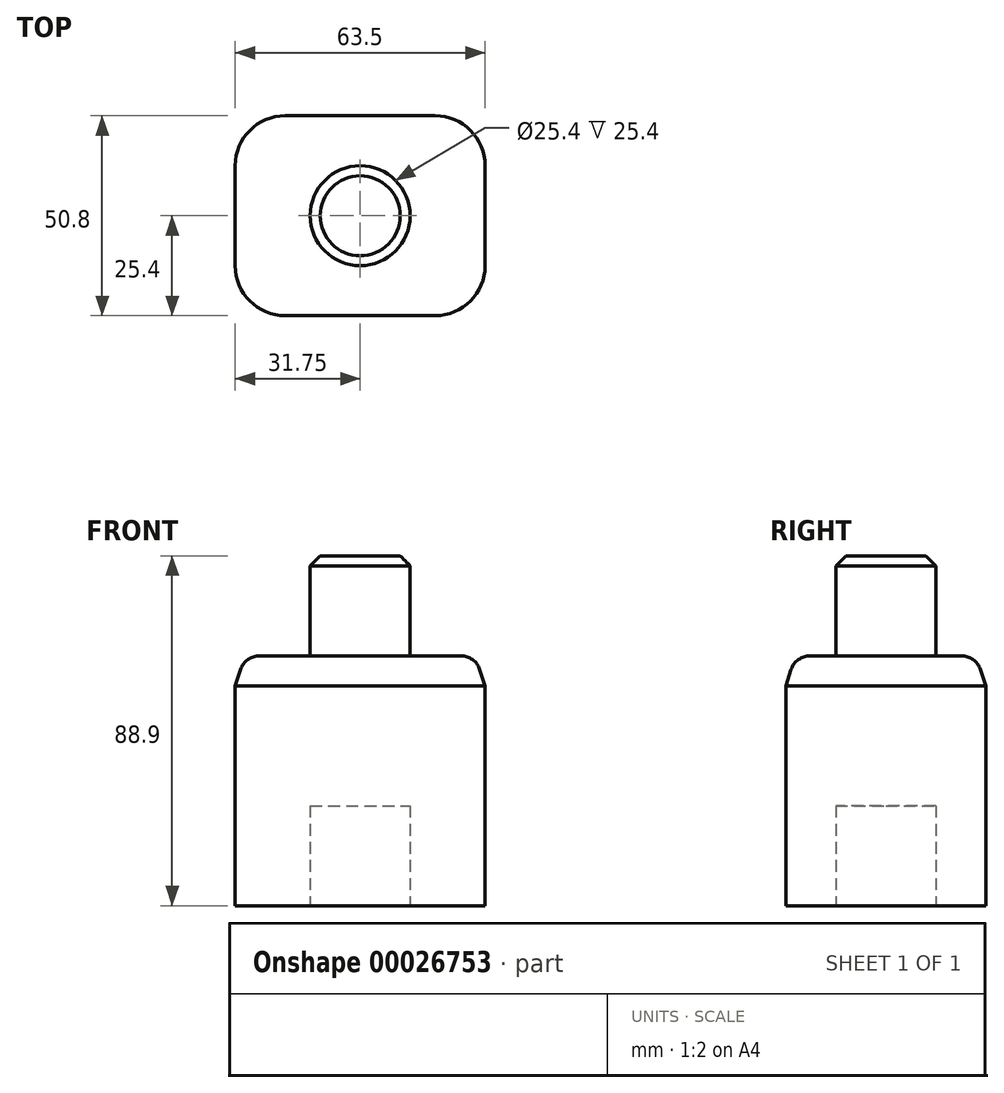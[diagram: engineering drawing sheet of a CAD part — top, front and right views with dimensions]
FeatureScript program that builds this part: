
annotation { "Feature Type Name" : "Feature", "Feature Type Description" : "" }
export const myFeature = defineFeature(function(context is Context, id is Id, definition is map)
    precondition{}
    {
        {
            var Q0;
            Q0=qCreatedBy(makeId("Front.planeOp"),FACE);
            var sketch = newSketch(context, id + "F0", { "sketchPlane" : qUnion([Q0])});
            skLineSegment(sketch, "E0.rect.bottom", {"start": v(31.75, 31.75) * mm, "end": v(-31.75, 31.75) * mm});
            skLineSegment(sketch, "E0.rect.top", {"start": v(31.75, -31.75) * mm, "end": v(-31.75, -31.75) * mm});
            skLineSegment(sketch, "E0.rect.left", {"start": v(31.75, 31.75) * mm, "end": v(31.75, -31.75) * mm});
            skLineSegment(sketch, "E0.rect.right", {"start": v(-31.75, 31.75) * mm, "end": v(-31.75, -31.75) * mm});
            skPoint(sketch, "E0.rect.middle", {"position": v(0, 0) * mm});
            skSolve(sketch);
        }
        {
            var Q0;
            Q0=makeQuery(id+"F0.imprint","IMPRINT",FACE,{"disambiguationData":[TD([[makeQuery(id+"F0.imprint","IMPRINT",EDGE,{"derivedFrom":sQuery(id+"F0.wireOp",EDGE,"E0.rect.bottom")}),1.0]])]});
            extrude(context, id + "F1", {"entities" : qUnion([Q0]), "depth" : 50.8 * mm});
        }
        {
            var Q0;
            Q0=makeQuery(id+"F1.opExtrude","CAP_EDGE",EDGE,{"disambiguationData":[OSD([sQuery(id+"F0.wireOp",EDGE,"E0.rect.right")])],"isStart":false});
            var Q1;
            Q1=makeQuery(id+"F1.opExtrude","CAP_EDGE",EDGE,{"disambiguationData":[OSD([sQuery(id+"F0.wireOp",EDGE,"E0.rect.left")])],"isStart":false});
            var Q2;
            Q2=makeQuery(id+"F1.opExtrude","CAP_EDGE",EDGE,{"disambiguationData":[OSD([sQuery(id+"F0.wireOp",EDGE,"E0.rect.left")])],"isStart":true});
            var Q3;
            Q3=makeQuery(id+"F1.opExtrude","CAP_EDGE",EDGE,{"disambiguationData":[OSD([sQuery(id+"F0.wireOp",EDGE,"E0.rect.right")])],"isStart":true});
            fillet(context, id + "F2", {"entities" : qUnion([Q0, Q1, Q2, Q3]), "radius" : 12.7 * mm, "tangentPropagation" : true, "allowEdgeOverflow" : false});
        }
        {
            var Q0;
            Q0=makeQuery(id+"F1.opExtrude","CAP_EDGE",EDGE,{"disambiguationData":[OSD([sQuery(id+"F0.wireOp",EDGE,"E0.rect.bottom")])],"isStart":true});
            chamfer(context, id + "F3", {"entities" : qUnion([Q0]), "chamferType" : ChamferType.TWO_OFFSETS, "width1" : 2.54 * mm, "oppositeDirection" : false, "width2" : 7.62 * mm, "tangentPropagation" : true});
        }
        {
            var Q0;
            Q0=makeQuery(id+"F1.opExtrude","SWEPT_FACE",FACE,{"disambiguationData":[OSD([sQuery(id+"F0.wireOp",EDGE,"E0.rect.top")])]});
            var sketch = newSketch(context, id + "F4", { "sketchPlane" : qUnion([Q0])});
            skCircle(sketch, "E1", {"center": v(0, 25.4) * mm, "radius": 12.7 * mm});
            skSolve(sketch);
        }
        {
            var Q0;
            Q0=makeQuery(id+"F4.imprint","IMPRINT",FACE,{"disambiguationData":[TD([[makeQuery(id+"F4.imprint","IMPRINT",EDGE,{"derivedFrom":sQuery(id+"F4.wireOp",EDGE,"E1")}),1.0]])]});
            extrude(context, id + "F5", {"entities" : qUnion([Q0]), "operationType" : NewBodyOperationType.REMOVE, "oppositeDirection" : true, "depth" : 25.4 * mm});
        }
        {
            var Q0;
            Q0=makeQuery(id+"F1.opExtrude","SWEPT_FACE",FACE,{"disambiguationData":[OSD([sQuery(id+"F0.wireOp",EDGE,"E0.rect.bottom")])]});
            var sketch = newSketch(context, id + "F6", { "sketchPlane" : qUnion([Q0])});
            skCircle(sketch, "E2", {"center": v(0, -25.4) * mm, "radius": 12.7 * mm});
            skLineSegment(sketch, "E3", {"start": v(0, -12.7) * mm, "end": v(0, -38.1) * mm});
            skSolve(sketch);
        }
        {
            var Q0;
            {var subQ0=sQuery(id+"F6.wireOp",EDGE,"E3");Q0=makeQuery(id+"F6.imprint","IMPRINT",FACE,{"disambiguationData":[TD([[makeQuery(id+"F6.imprint","IMPRINT",EDGE,{"derivedFrom":subQ0}),-1.0]])]});}
            var Q1;
            Q1=sQuery(id+"F6.wireOp",EDGE,"E3");
            revolve(context, id + "F7", {"entities" : qUnion([Q0]), "axis" : qUnion([Q1]), "revolveType" : RevolveType.FULL});
        }
        {
            var Q0;
            Q0=makeQuery(id+"F7.opRevolve","SWEPT_BODY",BODY,{"disambiguationData":[OSD([sQuery(id+"F6.wireOp",EDGE,"E2"),sQuery(id+"F6.wireOp",EDGE,"E3")])]});
            deleteBodies(context, id + "F8", {"entities" : qUnion([Q0])});
        }
        {
            var Q0;
            {var subQ0=sQuery(id+"F6.wireOp",EDGE,"E3");Q0=makeQuery(id+"F6.imprint","IMPRINT",FACE,{"disambiguationData":[TD([[makeQuery(id+"F6.imprint","IMPRINT",EDGE,{"derivedFrom":subQ0}),1.0]])]});}
            var Q1;
            {var subQ0=sQuery(id+"F6.wireOp",EDGE,"E3");Q1=makeQuery(id+"F6.imprint","IMPRINT",FACE,{"disambiguationData":[TD([[makeQuery(id+"F6.imprint","IMPRINT",EDGE,{"derivedFrom":subQ0}),-1.0]])]});}
            extrude(context, id + "F9", {"entities" : qUnion([Q0, Q1]), "operationType" : NewBodyOperationType.ADD, "depth" : 25.4 * mm});
        }
        {
            var Q0;
            Q0=makeQuery(id+"F9.opExtrude","CAP_EDGE",EDGE,{"disambiguationData":[OSD([sQuery(id+"F6.wireOp",EDGE,"E2")])],"isStart":false});
            chamfer(context, id + "F10", {"entities" : qUnion([Q0]), "width" : 2.54 * mm, "tangentPropagation" : true});
        }
        {
            var Q0;
            {var subQ0=sQuery(id+"F0.wireOp",EDGE,"E0.rect.bottom");Q0=makeQuery(id+"F3.opChamfer","BLEND_EDGE",EDGE,{"blendedFrom":[makeQuery(id+"F1.opExtrude","CAP_EDGE",EDGE,{"disambiguationData":[OSD([subQ0])],"isStart":true}),makeQuery(id+"F1.opExtrude","SWEPT_FACE",FACE,{"disambiguationData":[OSD([subQ0])]})],"blendedInto":[makeQuery(id+"F1.opExtrude","SWEPT_FACE",FACE,{"disambiguationData":[OSD([subQ0])]})]});}
            var Q1;
            Q1=makeQuery(id+"F9.opExtrude","CAP_EDGE",EDGE,{"disambiguationData":[OSD([sQuery(id+"F6.wireOp",EDGE,"E2")])],"isStart":true});
            fillet(context, id + "F11", {"entities" : qUnion([Q0, Q1]), "radius" : 5.08 * mm, "tangentPropagation" : true, "allowEdgeOverflow" : false});
        }
    });
